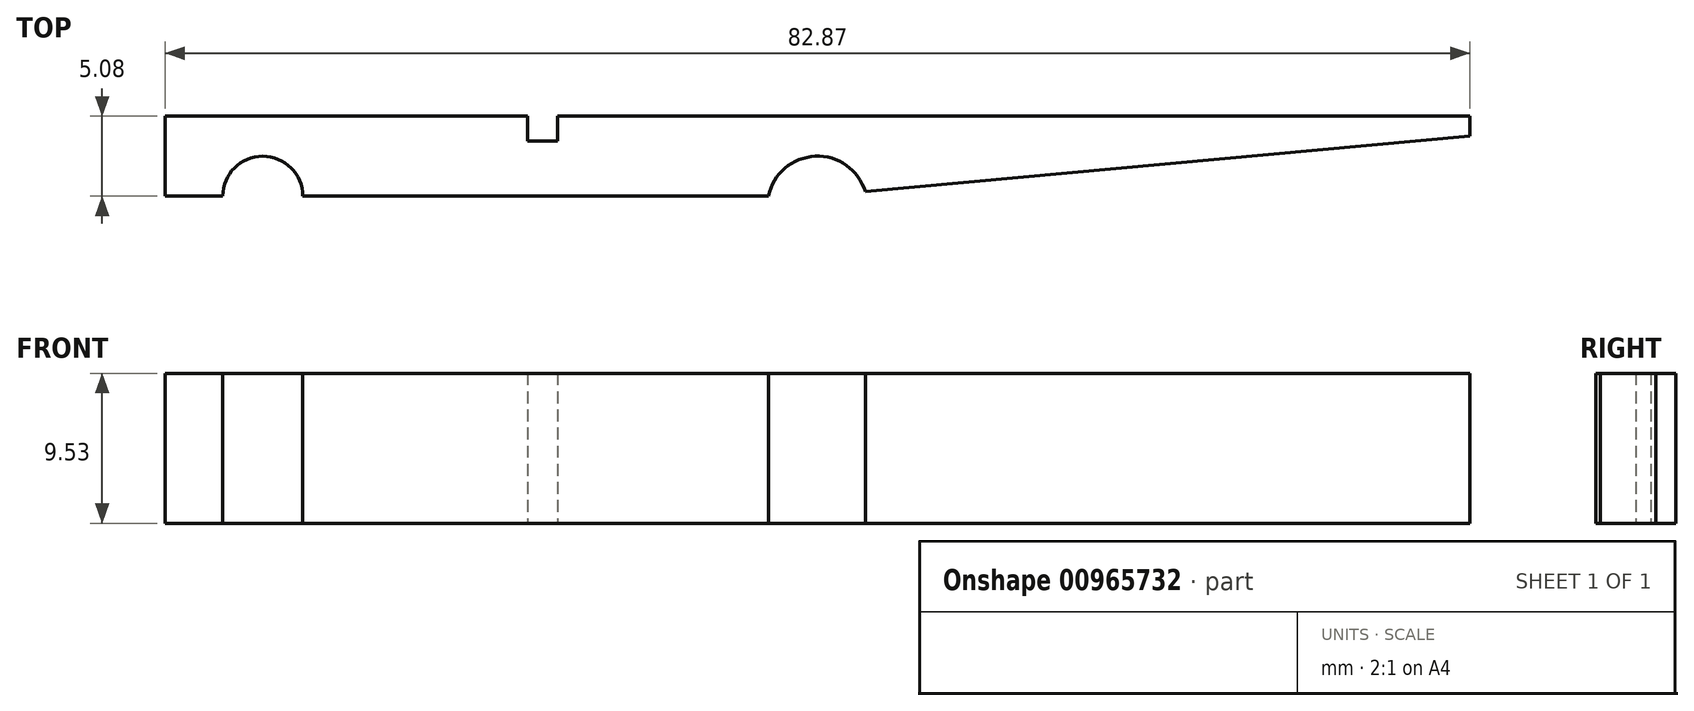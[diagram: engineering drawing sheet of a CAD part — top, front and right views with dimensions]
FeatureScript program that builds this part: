
annotation { "Feature Type Name" : "Feature", "Feature Type Description" : "" }
export const myFeature = defineFeature(function(context is Context, id is Id, definition is map)
    precondition{}
    {
        {
            var Q0;
            Q0=qCreatedBy(makeId("Top.planeOp"),FACE);
            var sketch = newSketch(context, id + "F0", { "sketchPlane" : qUnion([Q0])});
            skLineSegment(sketch, "E0.bottom", {"start": v(-33.05, 12.9) * mm, "end": v(-10.03, 12.9) * mm});
            skLineSegment(sketch, "E0.top", {"start": v(-33.05, 7.82) * mm, "end": v(-29.4, 7.82) * mm});
            skLineSegment(sketch, "E0.left", {"start": v(-33.05, 12.9) * mm, "end": v(-33.05, 7.82) * mm});
            skLineSegment(sketch, "E0.right", {"start": v(49.82, 12.9) * mm, "end": v(49.82, 11.63) * mm});
            skLineSegment(sketch, "E1", {"start": v(11.42, 8.1) * mm, "end": v(49.82, 11.63) * mm});
            skPoint(sketch, "E2.orphan", {"position": v(49.82, 7.82) * mm});
            skArc(sketch, "E3", {"start": v(-24.31, 7.82) * mm, "mid": v(-26.85, 10.36) * mm, "end": v(-29.4, 7.82) * mm});
            skLineSegment(sketch, "E4.trimOffspring", {"start": v(-24.31, 7.82) * mm, "end": v(5.27, 7.82) * mm});
            skLineSegment(sketch, "E5.top", {"start": v(-10.03, 11.31) * mm, "end": v(-8.12, 11.31) * mm});
            skLineSegment(sketch, "E5.left", {"start": v(-10.03, 12.9) * mm, "end": v(-10.03, 11.31) * mm});
            skLineSegment(sketch, "E5.right", {"start": v(-8.12, 12.9) * mm, "end": v(-8.12, 11.31) * mm});
            skLineSegment(sketch, "E6", {"start": v(-9.07, 11.31) * mm, "end": v(-9.07, 14.45) * mm, "construction": true});
            skLineSegment(sketch, "E7.trimOffspring", {"start": v(-8.12, 12.9) * mm, "end": v(49.82, 12.9) * mm});
            skArc(sketch, "E8", {"start": v(11.42, 8.1) * mm, "mid": v(8.24, 10.36) * mm, "end": v(5.27, 7.82) * mm});
            skSolve(sketch);
        }
        {
            var Q0;
            Q0 = qSketchRegion(id + "F0", true);
            extrude(context, id + "F1", {"entities" : qUnion([Q0]), "depth" : 9.52 * mm, "offsetDistance" : 25.4 * mm});
        }
    });
